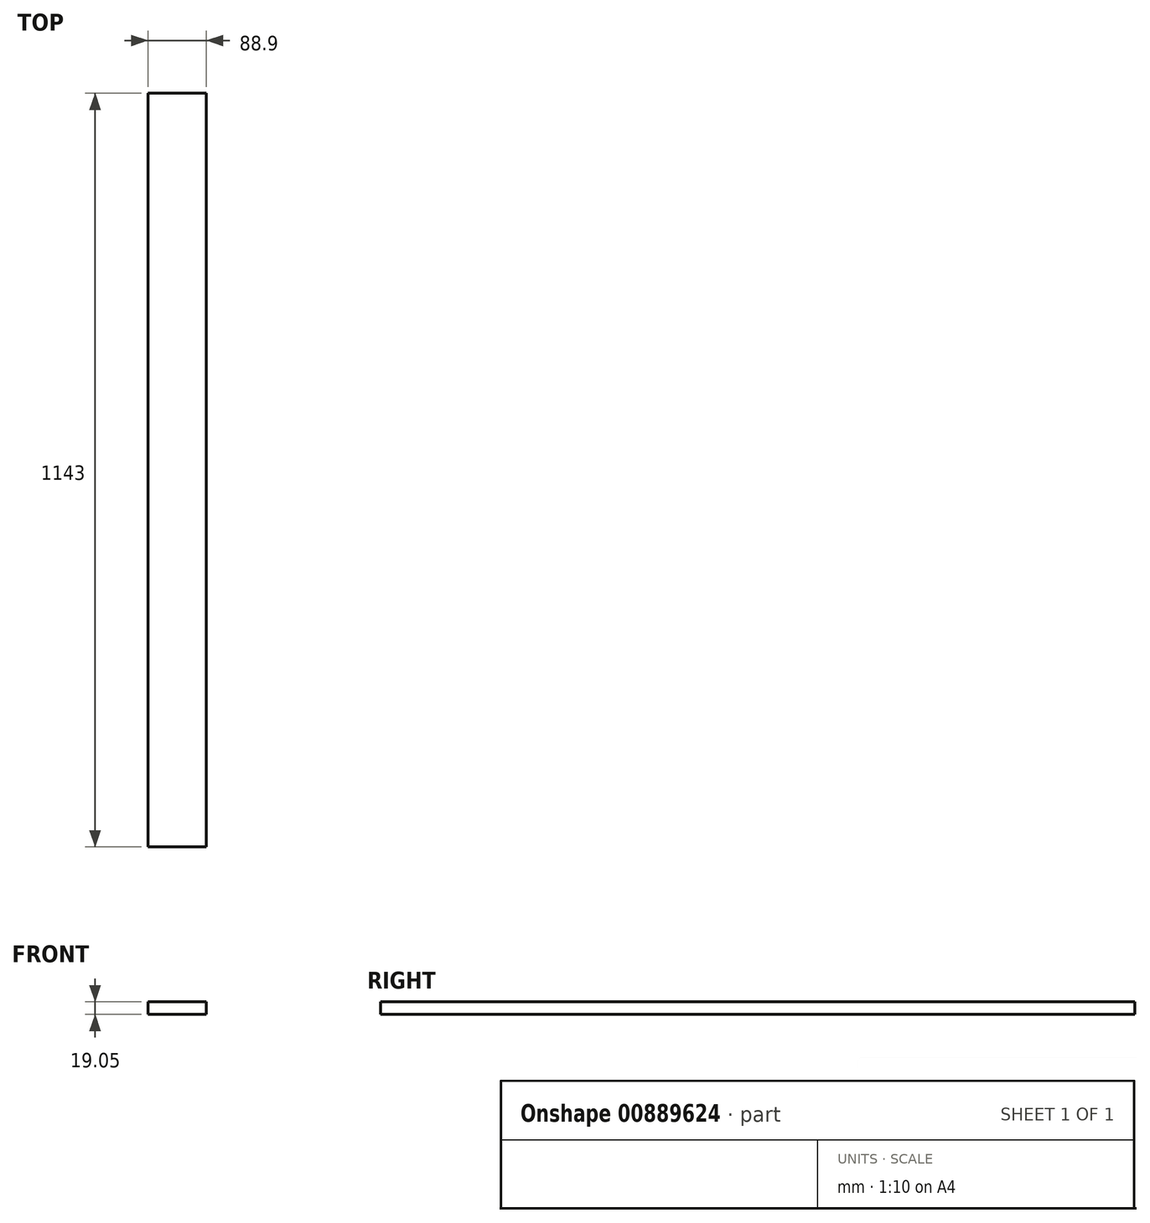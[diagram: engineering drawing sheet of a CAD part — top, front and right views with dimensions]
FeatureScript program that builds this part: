
annotation { "Feature Type Name" : "Feature", "Feature Type Description" : "" }
export const myFeature = defineFeature(function(context is Context, id is Id, definition is map)
    precondition{}
    {
        {
            var Q0;
            Q0=qCreatedBy(makeId("Top.planeOp"),FACE);
            var sketch = newSketch(context, id + "F0", { "sketchPlane" : qUnion([Q0])});
            skLineSegment(sketch, "E0.bottom", {"start": v(0, 0) * mm, "end": v(88.9, 0) * mm});
            skLineSegment(sketch, "E0.top", {"start": v(0, 1143) * mm, "end": v(88.9, 1143) * mm});
            skLineSegment(sketch, "E0.left", {"start": v(0, 0) * mm, "end": v(0, 1143) * mm});
            skLineSegment(sketch, "E0.right", {"start": v(88.9, 0) * mm, "end": v(88.9, 1143) * mm});
            skSolve(sketch);
        }
        {
            var Q0;
            Q0 = qSketchRegion(id + "F0", true);
            extrude(context, id + "F1", {"entities" : qUnion([Q0]), "depth" : 19.05 * mm, "offsetDistance" : 25.4 * mm});
        }
    });
